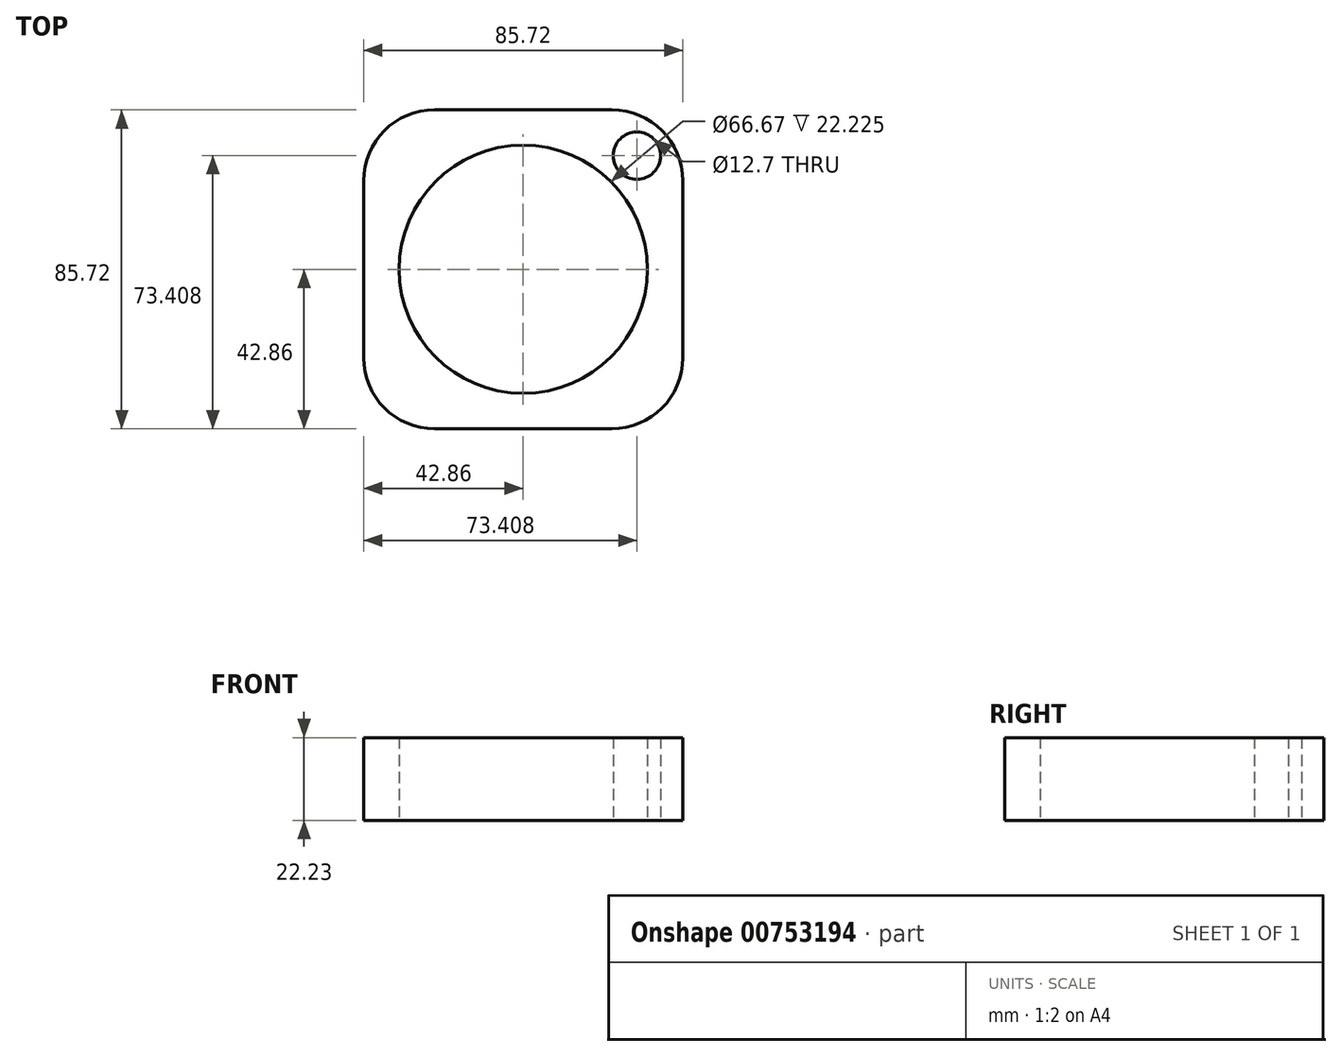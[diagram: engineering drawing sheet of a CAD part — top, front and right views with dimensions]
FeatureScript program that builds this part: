
annotation { "Feature Type Name" : "Feature", "Feature Type Description" : "" }
export const myFeature = defineFeature(function(context is Context, id is Id, definition is map)
    precondition{}
    {
        {
            var Q0;
            Q0=qCreatedBy(makeId("Top.planeOp"),FACE);
            var sketch = newSketch(context, id + "F0", { "sketchPlane" : qUnion([Q0])});
            skLineSegment(sketch, "E0.bottom", {"start": v(-23.81, -42.86) * mm, "end": v(23.81, -42.86) * mm});
            skLineSegment(sketch, "E0.top", {"start": v(-23.81, 42.86) * mm, "end": v(23.81, 42.86) * mm});
            skLineSegment(sketch, "E0.left", {"start": v(-42.86, -23.81) * mm, "end": v(-42.86, 23.81) * mm});
            skLineSegment(sketch, "E0.right", {"start": v(42.86, -23.81) * mm, "end": v(42.86, 23.81) * mm});
            skPoint(sketch, "E0.middle", {"position": v(0, 0) * mm});
            skCircle(sketch, "E1", {"center": v(0, 0) * mm, "radius": 33.34 * mm});
            skPoint(sketch, "E2.visualSharp", {"position": v(-42.86, 42.86) * mm});
            skArc(sketch, "E2.filletArc", {"start": v(-23.81, 42.86) * mm, "mid": v(-37.28, 37.28) * mm, "end": v(-42.86, 23.81) * mm});
            skPoint(sketch, "E3.visualSharp", {"position": v(42.86, 42.86) * mm});
            skArc(sketch, "E3.filletArc", {"start": v(42.86, 23.81) * mm, "mid": v(37.28, 37.28) * mm, "end": v(23.81, 42.86) * mm});
            skPoint(sketch, "E4.visualSharp", {"position": v(42.86, -42.86) * mm});
            skArc(sketch, "E4.filletArc", {"start": v(23.81, -42.86) * mm, "mid": v(37.28, -37.28) * mm, "end": v(42.86, -23.81) * mm});
            skPoint(sketch, "E5.visualSharp", {"position": v(-42.86, -42.86) * mm});
            skArc(sketch, "E5.filletArc", {"start": v(-42.86, -23.81) * mm, "mid": v(-37.28, -37.28) * mm, "end": v(-23.81, -42.86) * mm});
            skCircle(sketch, "E6", {"center": v(30.55, 30.55) * mm, "radius": 6.35 * mm});
            skLineSegment(sketch, "E7", {"start": v(42.86, 42.86) * mm, "end": v(23.81, 23.81) * mm, "construction": true});
            skSolve(sketch);
        }
        {
            var Q0;
            Q0 = qSketchRegion(id + "F0", true);
            var Q1;
            Q1=makeQuery(id+"F0.imprint","IMPRINT",FACE,{"disambiguationData":[TD([[makeQuery(id+"F0.imprint","IMPRINT",EDGE,{"derivedFrom":sQuery(id+"F0.wireOp",EDGE,"E0.bottom")}),1.0]])]});
            extrude(context, id + "F1", {"entities" : qUnion([Q0, Q1]), "depth" : 22.22 * mm, "offsetDistance" : 25.4 * mm});
        }
    });
